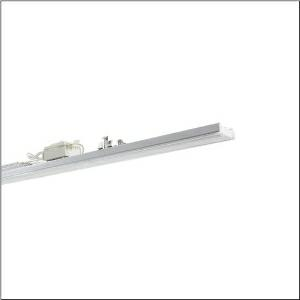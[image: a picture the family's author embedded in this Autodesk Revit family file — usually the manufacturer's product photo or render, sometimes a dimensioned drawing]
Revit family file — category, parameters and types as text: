
# Revit family: licross_r__11_recessed_mo_51tl10dv4e5g_4b08
name_source: partatom
category: Lighting Fixtures
units: mm (PartAtom-declared; Revit-internal decimal feet)

## family parameters
Cut with Voids When Loaded = No
Host = Face
Light Source = No
Part Type = Normal
Room Calculation Point = No
Round Connector Dimension = Use Diameter
Shared = No

## types (1)
- --- (1 x LED, 14930 lm, 84.1 W, 4000K)
    Apparent Load = 84 VA
    CIE Flux Codes = 50 81 96 100 100
    Color Rendering = 80
    Color Temperature = 4000K
    Default Elevation = 1800 mm
    Description = Licross® 11 Recessed MO, luminaire insert, of sheet steel, coil coated, white, length: 2.250mm, width: 66mm, height: 67mm, LED rated luminous flux: 14.930lm, light colour: 840, control gear: DALI 2, with plug, 5-pole, with phase selection, mains connection: 220..240V, AC, 50/60Hz, rated input power: 84W, halogen-free wiring, primary optical cover: cover, of PMMA, light emission: direct distribution, primary light characteristic: symmetric, protection rating (complete): IP40, insulation class (complete): insulation class I (protective earthing), certification: CE, ENEC, VDE, UKCA, protection symbol: D if used in an environment without relevant dust loads with corresponding accessories, impact resistance: IK06, permissible ambient temperature for indoor applications: -25..+35°C, corresponds to IFS (International Featured Standards) requirements for safety and quality in the food industry, reducing of maximum allowable ambient temperature of 5°C with ceiling mounting, LABS conformity tested according to VDMA 24364:2018-05, packaging unit: 1 piece
    Height = 58 mm
    Lamp = 1 x LED
    Lamp Light Flux = 14930 lm
    Lamp Power = 84.1 W
    Lamp count = 1
    Length = 2250 mm
    Luminous efficacy = 178 lm/W
    Manufacturer = Siteco
    ModVariant = No
    Model = 51TL10DV4E5G
    Mounting Place = Ceiling
    Mounting Type = Pendant
    Number of Poles = 1
    OnlyDefault = Yes
    Power Factor = 1
    Product Name = Licross® 11 Recessed MO
    Product group = luminaire insert
    ProductGroupID = 902
    Protection Class = Protection class I
    Protection Degree = IP 40
    RLX_Detail_Level = 1
    RLX_Emergency_Light_Flux = 0 lm
    RLX_Emergency_Type = 0
    RLX_Emergency_Type_DB = No
    RlxData = <blob elided: 28973 chars, md5=04421f20>
    Socket = socket
    Standby Power = 0 W
    System Light Flux = 14930 lm
    System Power = 84 W
    Type Comments = factory setting: luminous flux: 100 % | dim-lin: 254 | 378 mA
    Type Image = l_1296930.jpg
    URL = http://relux.com
    VarID = @adj_099816
    Voltage = 0 V
    Weight = 0.00 kg
    Width = 66 mm

## geometry (parser evidence)
native form markers: Blend x4, Sweep x10
no freeform markers — native parametric forms only
